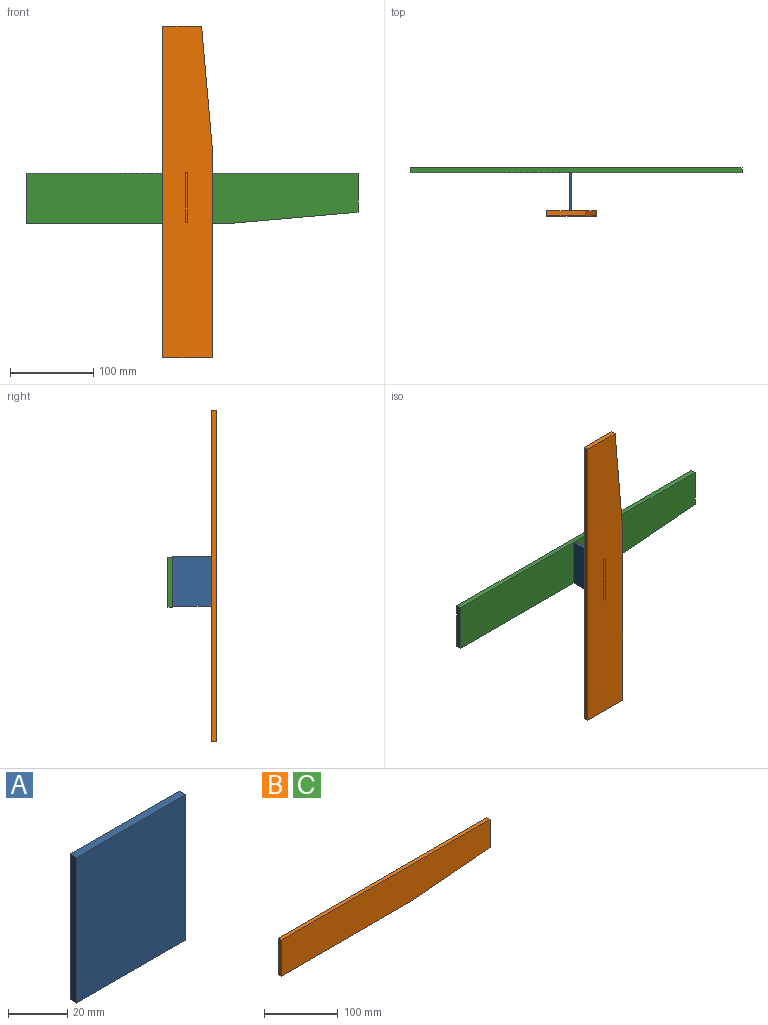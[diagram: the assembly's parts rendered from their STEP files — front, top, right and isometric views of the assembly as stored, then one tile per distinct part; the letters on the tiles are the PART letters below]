
ASSEMBLY  parts=3 mates=1
PART A: 6 faces, bbox 52x3x60 mm
  f0: plane 60x3mm, normal (-1,0,0), area 180mm2, adj f1,f3,f4,f5
  f1: plane 52x3mm, normal (0,0,-1), area 156mm2, adj f0,f2,f4,f5
  f2: plane 60x3mm, normal (1,0,0), area 180mm2, adj f1,f3,f4,f5
  f3: plane 52x3mm, normal (0,0,1), area 156mm2, adj f0,f2,f4,f5
  f4: plane 60x52mm, normal (0,-1,0), area 3120mm2, adj f0,f1,f2,f3
  f5: plane 60x52mm, normal (0,1,0), area 3120mm2, adj f0,f1,f2,f3
PART B: 7 faces, bbox 400x6x60 mm
  f0: plane 60x6mm, normal (-1,0,0), area 360mm2, adj f1,f4,f5,f6
  f1: plane 250x6mm, normal (0,0,-1), area 1500mm2, adj f0,f2,f5,f6
  f2: plane 150x13.12mm, normal (0.09,0,-1), area 903.4mm2, adj f1,f3,f5,f6
  f3: plane 46.88x6mm, normal (1,0,0), area 281.3mm2, adj f2,f4,f5,f6
  f4: plane 400x6mm, normal (0,0,1), area 2400mm2, adj f0,f3,f5,f6
  f5: plane 400x60mm, normal (0,-1,0), area 23015.8mm2, adj f0,f1,f2,f3,f4
  f6: plane 400x60mm, normal (0,1,0), area 23015.8mm2, adj f0,f1,f2,f3,f4
PART C: same geometry as B
PLACE A rot(axis=(0,0,-1),90deg) t=(32.11,125.67,-50.73)mm
PLACE B rot(axis=(0,-1,0),90deg) t=(61.71,79.67,-214.32)mm
PLACE C t=(-162.98,131.67,-51.83)mm
MATE fastened A.f0 <-> C.f5  axis (0,1,0) through (30.61,125.67,-20.73)mm
